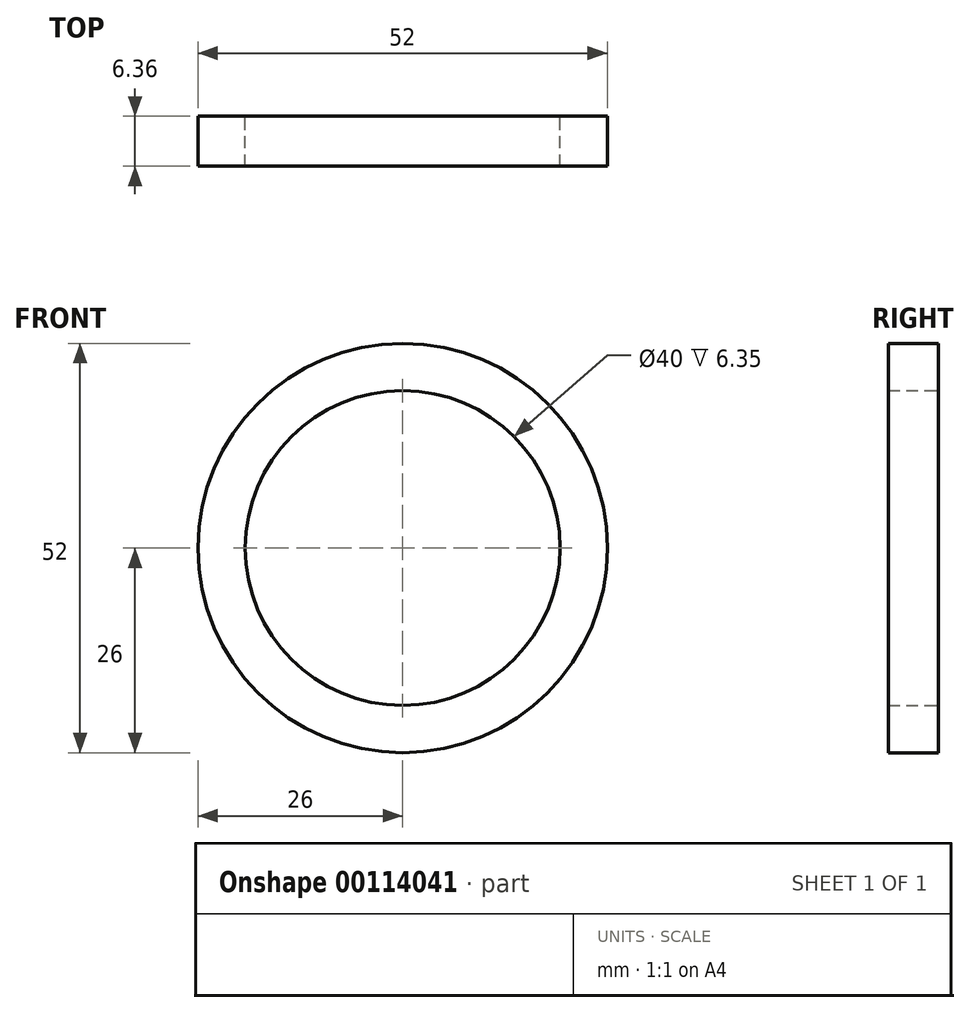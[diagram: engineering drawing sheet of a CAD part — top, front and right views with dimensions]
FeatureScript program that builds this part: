
annotation { "Feature Type Name" : "Feature", "Feature Type Description" : "" }
export const myFeature = defineFeature(function(context is Context, id is Id, definition is map)
    precondition{}
    {
        {
            var Q0;
            Q0=qCreatedBy(makeId("Front.planeOp"),FACE);
            var sketch = newSketch(context, id + "F0", { "sketchPlane" : qUnion([Q0])});
            skCircle(sketch, "E0", {"center": v(0, 0) * mm, "radius": 20 * mm});
            skCircle(sketch, "E1", {"center": v(0, 0) * mm, "radius": 26 * mm});
            skSolve(sketch);
        }
        {
            var Q0;
            Q0=makeQuery(id+"F0.imprint","IMPRINT",FACE,{"disambiguationData":[TD([[makeQuery(id+"F0.imprint","IMPRINT",EDGE,{"derivedFrom":sQuery(id+"F0.wireOp",EDGE,"E0")}),-1.0]])]});
            extrude(context, id + "F1", {"entities" : qUnion([Q0]), "endBound" : BoundingType.SYMMETRIC, "depth" : 6.35 * mm});
        }
    });
